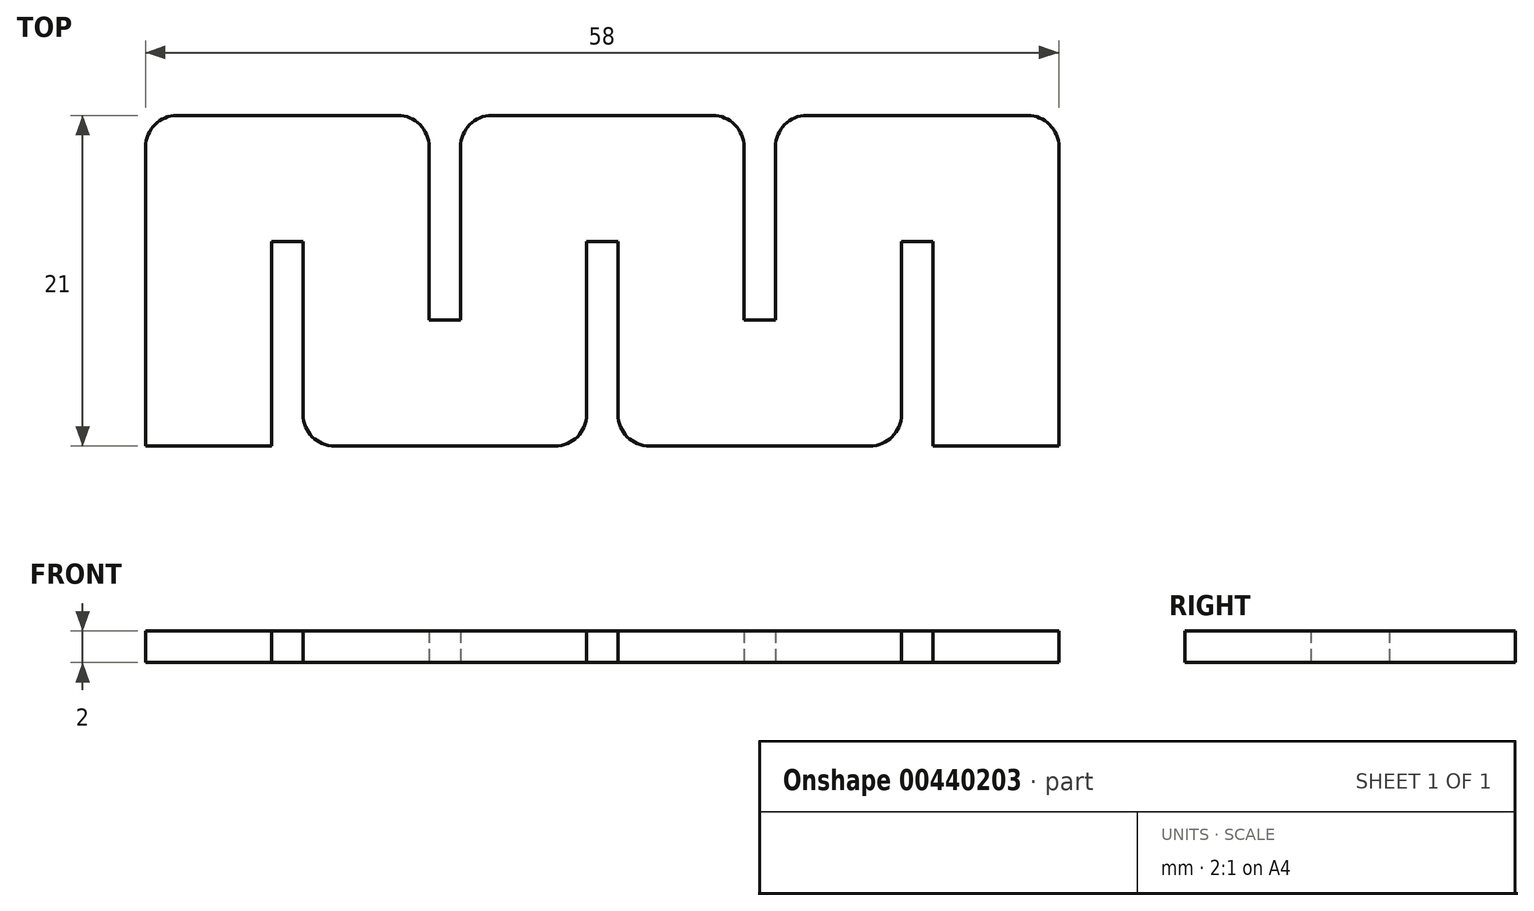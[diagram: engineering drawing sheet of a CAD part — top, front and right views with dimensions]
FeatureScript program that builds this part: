
annotation { "Feature Type Name" : "Feature", "Feature Type Description" : "" }
export const myFeature = defineFeature(function(context is Context, id is Id, definition is map)
    precondition{}
    {
        {
            var Q0;
            Q0=qCreatedBy(makeId("Top.planeOp"),FACE);
            var sketch = newSketch(context, id + "F0", { "sketchPlane" : qUnion([Q0])});
            skLineSegment(sketch, "E0.bottom", {"start": v(31, 12.5) * mm, "end": v(-31, 12.5) * mm});
            skLineSegment(sketch, "E0.top", {"start": v(31, -12.5) * mm, "end": v(-31, -12.5) * mm});
            skLineSegment(sketch, "E0.left", {"start": v(31, 12.5) * mm, "end": v(31, -12.5) * mm});
            skLineSegment(sketch, "E0.right", {"start": v(-31, 12.5) * mm, "end": v(-31, -12.5) * mm});
            skPoint(sketch, "E0.middle", {"position": v(0, 0) * mm});
            skSolve(sketch);
        }
        {
            var Q0;
            Q0=makeQuery(id+"F0.imprint","IMPRINT",FACE,{"disambiguationData":[TD([[makeQuery(id+"F0.imprint","IMPRINT",EDGE,{"derivedFrom":sQuery(id+"F0.wireOp",EDGE,"E0.bottom")}),1.0]])]});
            extrude(context, id + "F1", {"entities" : qUnion([Q0]), "depth" : 1 * mm});
        }
        {
            var Q0;
            Q0=makeQuery(id+"F1.opExtrude","CAP_FACE",FACE,{"disambiguationData":[OSD([sQuery(id+"F0.wireOp",EDGE,"E0.bottom"),sQuery(id+"F0.wireOp",EDGE,"E0.top"),sQuery(id+"F0.wireOp",EDGE,"E0.left"),sQuery(id+"F0.wireOp",EDGE,"E0.right")])],"isStart":false});
            var sketch = newSketch(context, id + "F2", { "sketchPlane" : qUnion([Q0])});
            skLineSegment(sketch, "E1.bottom", {"start": v(-31, 12.5) * mm, "end": v(31, 12.5) * mm});
            skLineSegment(sketch, "E1.top", {"start": v(-31, -12.5) * mm, "end": v(31, -12.5) * mm});
            skLineSegment(sketch, "E1.left", {"start": v(-31, 12.5) * mm, "end": v(-31, -12.5) * mm});
            skLineSegment(sketch, "E1.right", {"start": v(31, 12.5) * mm, "end": v(31, -12.5) * mm});
            skLineSegment(sketch, "E2.bottom", {"start": v(-27, 10.5) * mm, "end": v(-13, 10.5) * mm});
            skLineSegment(sketch, "E2.top", {"start": v(-29, -10.5) * mm, "end": v(-21, -10.5) * mm});
            skLineSegment(sketch, "E2.left", {"start": v(-29, 8.5) * mm, "end": v(-29, -10.5) * mm});
            skLineSegment(sketch, "E2.right", {"start": v(29, 8.5) * mm, "end": v(29, -10.5) * mm});
            skLineSegment(sketch, "E3.bottom", {"start": v(-21, 2.5) * mm, "end": v(-19, 2.5) * mm});
            skLineSegment(sketch, "E3.left", {"start": v(-21, 2.5) * mm, "end": v(-21, -10.5) * mm});
            skLineSegment(sketch, "E3.right", {"start": v(-19, 2.5) * mm, "end": v(-19, -8.5) * mm});
            skLineSegment(sketch, "E4.top", {"start": v(-11, -2.5) * mm, "end": v(-9, -2.5) * mm});
            skLineSegment(sketch, "E4.left", {"start": v(-11, 8.5) * mm, "end": v(-11, -2.5) * mm});
            skLineSegment(sketch, "E4.right", {"start": v(-9, 8.5) * mm, "end": v(-9, -2.5) * mm});
            skLineSegment(sketch, "E5.bottom", {"start": v(-1, 2.5) * mm, "end": v(1, 2.5) * mm});
            skLineSegment(sketch, "E5.left", {"start": v(-1, 2.5) * mm, "end": v(-1, -8.5) * mm});
            skLineSegment(sketch, "E5.right", {"start": v(1, 2.5) * mm, "end": v(1, -8.5) * mm});
            skLineSegment(sketch, "E6.top", {"start": v(9, -2.5) * mm, "end": v(11, -2.5) * mm});
            skLineSegment(sketch, "E6.left", {"start": v(9, 8.5) * mm, "end": v(9, -2.5) * mm});
            skLineSegment(sketch, "E6.right", {"start": v(11, 8.5) * mm, "end": v(11, -2.5) * mm});
            skLineSegment(sketch, "E7.bottom", {"start": v(19, 2.5) * mm, "end": v(21, 2.5) * mm});
            skLineSegment(sketch, "E7.left", {"start": v(19, 2.5) * mm, "end": v(19, -8.5) * mm});
            skLineSegment(sketch, "E7.right", {"start": v(21, 2.5) * mm, "end": v(21, -10.5) * mm});
            skLineSegment(sketch, "E8.trimOffspring", {"start": v(-7, 10.5) * mm, "end": v(7, 10.5) * mm});
            skLineSegment(sketch, "E9.trimOffspring", {"start": v(13, 10.5) * mm, "end": v(27, 10.5) * mm});
            skLineSegment(sketch, "E10.trimOffspring", {"start": v(-17, -10.5) * mm, "end": v(-3, -10.5) * mm});
            skLineSegment(sketch, "E11.trimOffspring", {"start": v(3, -10.5) * mm, "end": v(17, -10.5) * mm});
            skLineSegment(sketch, "E12.trimOffspring", {"start": v(21, -10.5) * mm, "end": v(29, -10.5) * mm});
            skPoint(sketch, "E13.visualSharp", {"position": v(-29, 10.5) * mm});
            skArc(sketch, "E13.filletArc", {"start": v(-27, 10.5) * mm, "mid": v(-28.41, 9.91) * mm, "end": v(-29, 8.5) * mm});
            skPoint(sketch, "E14.visualSharp", {"position": v(-11, 10.5) * mm});
            skArc(sketch, "E14.filletArc", {"start": v(-11, 8.5) * mm, "mid": v(-11.59, 9.91) * mm, "end": v(-13, 10.5) * mm});
            skPoint(sketch, "E15.visualSharp", {"position": v(-9, 10.5) * mm});
            skArc(sketch, "E15.filletArc", {"start": v(-7, 10.5) * mm, "mid": v(-8.41, 9.91) * mm, "end": v(-9, 8.5) * mm});
            skPoint(sketch, "E16.visualSharp", {"position": v(9, 10.5) * mm});
            skArc(sketch, "E16.filletArc", {"start": v(9, 8.5) * mm, "mid": v(8.41, 9.91) * mm, "end": v(7, 10.5) * mm});
            skPoint(sketch, "E17.visualSharp", {"position": v(11, 10.5) * mm});
            skArc(sketch, "E17.filletArc", {"start": v(13, 10.5) * mm, "mid": v(11.59, 9.91) * mm, "end": v(11, 8.5) * mm});
            skPoint(sketch, "E18.visualSharp", {"position": v(1, -10.5) * mm});
            skArc(sketch, "E18.filletArc", {"start": v(1, -8.5) * mm, "mid": v(1.59, -9.91) * mm, "end": v(3, -10.5) * mm});
            skPoint(sketch, "E19.visualSharp", {"position": v(-19, -10.5) * mm});
            skArc(sketch, "E19.filletArc", {"start": v(-19, -8.5) * mm, "mid": v(-18.41, -9.91) * mm, "end": v(-17, -10.5) * mm});
            skPoint(sketch, "E20.visualSharp", {"position": v(-1, -10.5) * mm});
            skArc(sketch, "E20.filletArc", {"start": v(-3, -10.5) * mm, "mid": v(-1.59, -9.91) * mm, "end": v(-1, -8.5) * mm});
            skPoint(sketch, "E21.visualSharp", {"position": v(19, -10.5) * mm});
            skArc(sketch, "E21.filletArc", {"start": v(17, -10.5) * mm, "mid": v(18.41, -9.91) * mm, "end": v(19, -8.5) * mm});
            skPoint(sketch, "E22.visualSharp", {"position": v(29, 10.5) * mm});
            skArc(sketch, "E22.filletArc", {"start": v(29, 8.5) * mm, "mid": v(28.41, 9.91) * mm, "end": v(27, 10.5) * mm});
            skSolve(sketch);
        }
        {
            var Q0;
            Q0=makeQuery(id+"F2.imprint","IMPRINT",FACE,{"disambiguationData":[TD([[makeQuery(id+"F2.imprint","IMPRINT",EDGE,{"derivedFrom":sQuery(id+"F2.wireOp",EDGE,"E2.bottom")}),-1.0]])]});
            extrude(context, id + "F3", {"entities" : qUnion([Q0]), "operationType" : NewBodyOperationType.ADD, "depth" : 2 * mm});
        }
        {
            var Q0;
            Q0=makeQuery(id+"F1.opExtrude","CAP_FACE",FACE,{"disambiguationData":[OSD([sQuery(id+"F0.wireOp",EDGE,"E0.bottom"),sQuery(id+"F0.wireOp",EDGE,"E0.top"),sQuery(id+"F0.wireOp",EDGE,"E0.left"),sQuery(id+"F0.wireOp",EDGE,"E0.right")])],"isStart":true});
            extrude(context, id + "F4", {"entities" : qUnion([Q0]), "operationType" : NewBodyOperationType.REMOVE, "oppositeDirection" : true, "depth" : 1 * mm});
        }
    });
